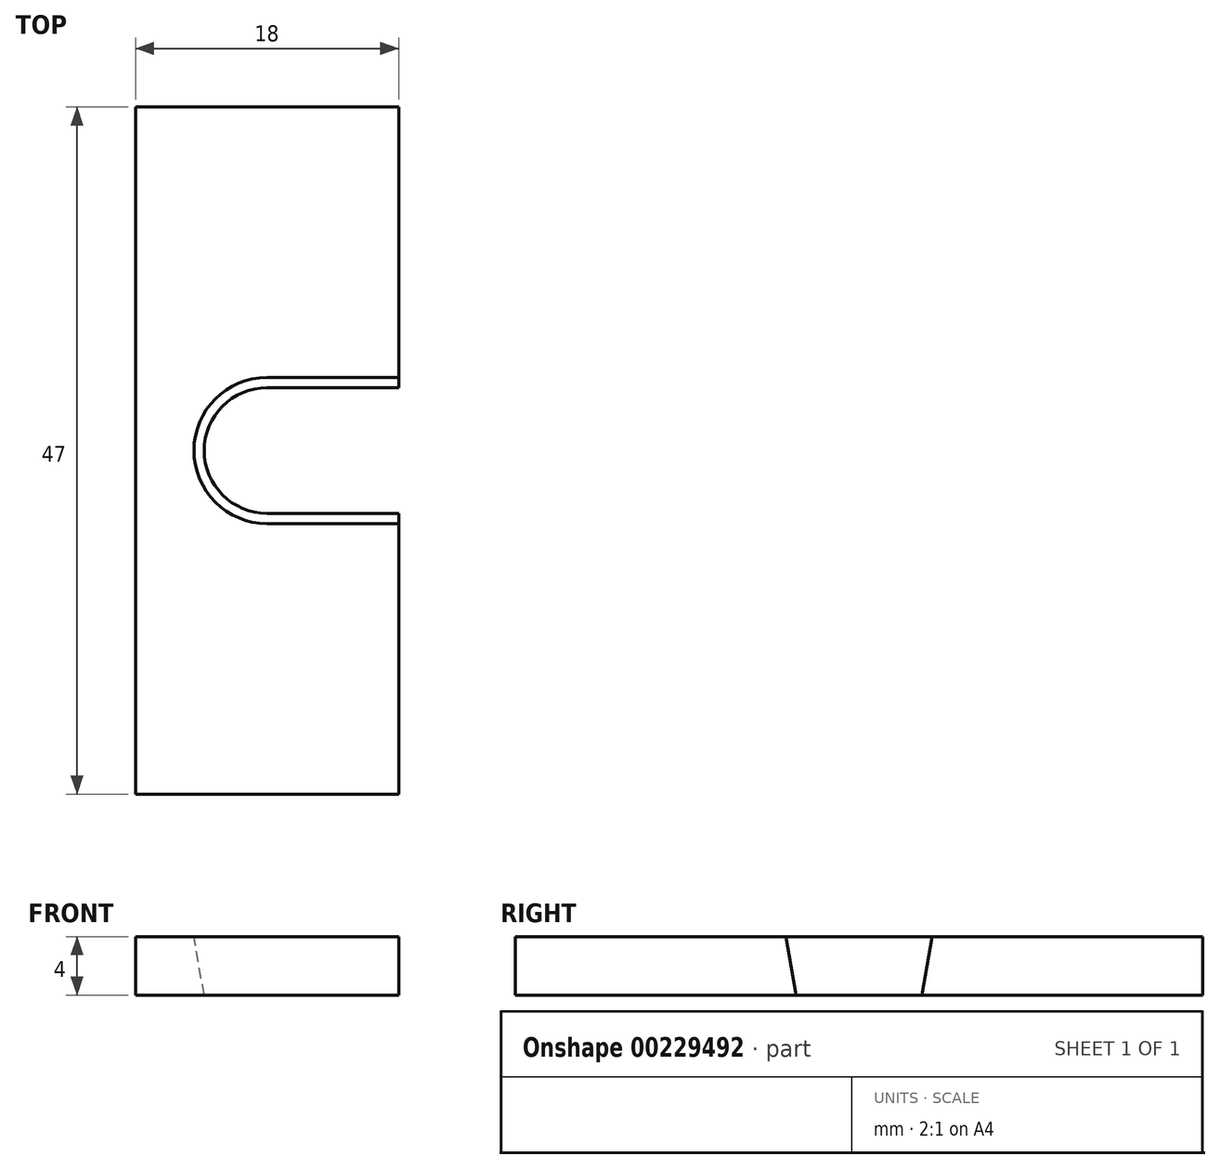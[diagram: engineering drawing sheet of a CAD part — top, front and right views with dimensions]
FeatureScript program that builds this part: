
annotation { "Feature Type Name" : "Feature", "Feature Type Description" : "" }
export const myFeature = defineFeature(function(context is Context, id is Id, definition is map)
    precondition{}
    {
        {
            var Q0;
            Q0=qCreatedBy(makeId("Top.planeOp"),FACE);
            var sketch = newSketch(context, id + "F0", { "sketchPlane" : qUnion([Q0])});
            skLineSegment(sketch, "E0.bottom", {"start": v(9, 23.5) * mm, "end": v(-9, 23.5) * mm});
            skLineSegment(sketch, "E0.top", {"start": v(9, -23.5) * mm, "end": v(-9, -23.5) * mm});
            skLineSegment(sketch, "E0.left", {"start": v(9, 23.5) * mm, "end": v(9, -23.5) * mm});
            skLineSegment(sketch, "E0.right", {"start": v(-9, 23.5) * mm, "end": v(-9, -23.5) * mm});
            skPoint(sketch, "E0.middle", {"position": v(0, 0) * mm});
            skSolve(sketch);
        }
        {
            var Q0;
            Q0=makeQuery(id+"F0.imprint","IMPRINT",FACE,{"disambiguationData":[TD([[makeQuery(id+"F0.imprint","IMPRINT",EDGE,{"derivedFrom":sQuery(id+"F0.wireOp",EDGE,"E0.bottom")}),1.0]])]});
            extrude(context, id + "F1", {"entities" : qUnion([Q0]), "depth" : 4 * mm});
        }
        {
            var Q0;
            Q0=makeQuery(id+"F1.opExtrude","CAP_FACE",FACE,{"disambiguationData":[OSD([sQuery(id+"F0.wireOp",EDGE,"E0.bottom"),sQuery(id+"F0.wireOp",EDGE,"E0.top"),sQuery(id+"F0.wireOp",EDGE,"E0.left"),sQuery(id+"F0.wireOp",EDGE,"E0.right")])],"isStart":false});
            var sketch = newSketch(context, id + "F2", { "sketchPlane" : qUnion([Q0])});
            skCircle(sketch, "E1", {"center": v(0, 0) * mm, "radius": 5 * mm});
            skLineSegment(sketch, "E2.bottom", {"start": v(0, 5) * mm, "end": v(10, 5) * mm});
            skLineSegment(sketch, "E2.top", {"start": v(0, -5) * mm, "end": v(10, -5) * mm});
            skLineSegment(sketch, "E2.left", {"start": v(0, 5) * mm, "end": v(0, -5) * mm});
            skLineSegment(sketch, "E2.right", {"start": v(10, 5) * mm, "end": v(10, -5) * mm});
            skPoint(sketch, "E2.middle", {"position": v(5, 0) * mm});
            skSolve(sketch);
        }
        {
            var Q0;
            Q0 = qSketchRegion(id + "F2", true);
            extrude(context, id + "F3", {"entities" : qUnion([Q0]), "operationType" : NewBodyOperationType.REMOVE, "oppositeDirection" : true, "depth" : 4 * mm, "hasDraft" : true, "draftAngle" : 10 * degree, "draftPullDirection" : true});
        }
    });
